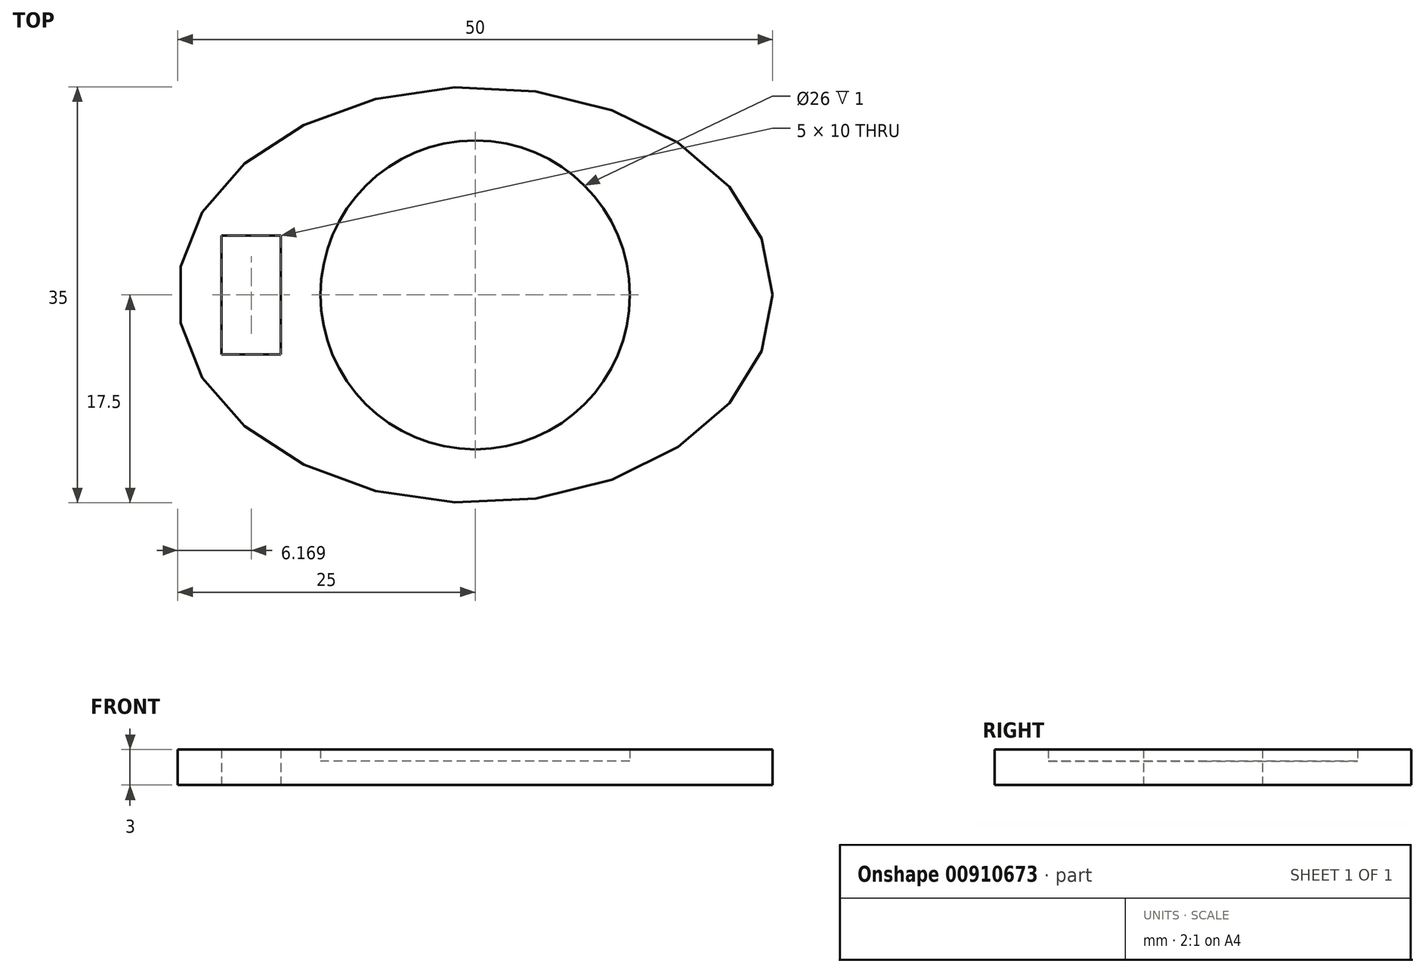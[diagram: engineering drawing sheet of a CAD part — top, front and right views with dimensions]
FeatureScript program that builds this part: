
annotation { "Feature Type Name" : "Feature", "Feature Type Description" : "" }
export const myFeature = defineFeature(function(context is Context, id is Id, definition is map)
    precondition{}
    {
        {
            var Q0;
            Q0=qCreatedBy(makeId("Top.planeOp"),FACE);
            var sketch = newSketch(context, id + "F0", { "sketchPlane" : qUnion([Q0])});
            skCircle(sketch, "E0", {"center": v(0, 0) * mm, "radius": 13 * mm});
            skEllipse(sketch, "E1", {"center": v(0, 0) * mm, "majorRadius": 25 * mm, "minorRadius": 17.5 * mm, "majorAxis": v(1, 0)});
            skLineSegment(sketch, "E2.bottom", {"start": v(-16.33, 5) * mm, "end": v(-21.33, 5) * mm});
            skLineSegment(sketch, "E2.top", {"start": v(-16.33, -5) * mm, "end": v(-21.33, -5) * mm});
            skLineSegment(sketch, "E2.left", {"start": v(-16.33, 5) * mm, "end": v(-16.33, -5) * mm});
            skLineSegment(sketch, "E2.right", {"start": v(-21.33, 5) * mm, "end": v(-21.33, -5) * mm});
            skPoint(sketch, "E2.middle", {"position": v(-18.83, 0) * mm});
            skSolve(sketch);
        }
        {
            var Q0;
            Q0=makeQuery(id+"F0.imprint","IMPRINT",FACE,{"disambiguationData":[TD([[makeQuery(id+"F0.imprint","IMPRINT",EDGE,{"derivedFrom":sQuery(id+"F0.wireOp",EDGE,"E0")}),1.0]])]});
            extrude(context, id + "F1", {"entities" : qUnion([Q0]), "depth" : 2 * mm, "offsetDistance" : 25 * mm});
        }
        {
            var Q0;
            Q0=makeQuery(id+"F0.imprint","IMPRINT",FACE,{"disambiguationData":[TD([[makeQuery(id+"F0.imprint","IMPRINT",EDGE,{"derivedFrom":sQuery(id+"F0.wireOp",EDGE,"E0")}),-1.0]])]});
            extrude(context, id + "F2", {"entities" : qUnion([Q0]), "operationType" : NewBodyOperationType.ADD, "depth" : 3 * mm, "offsetDistance" : 25 * mm});
        }
    });
